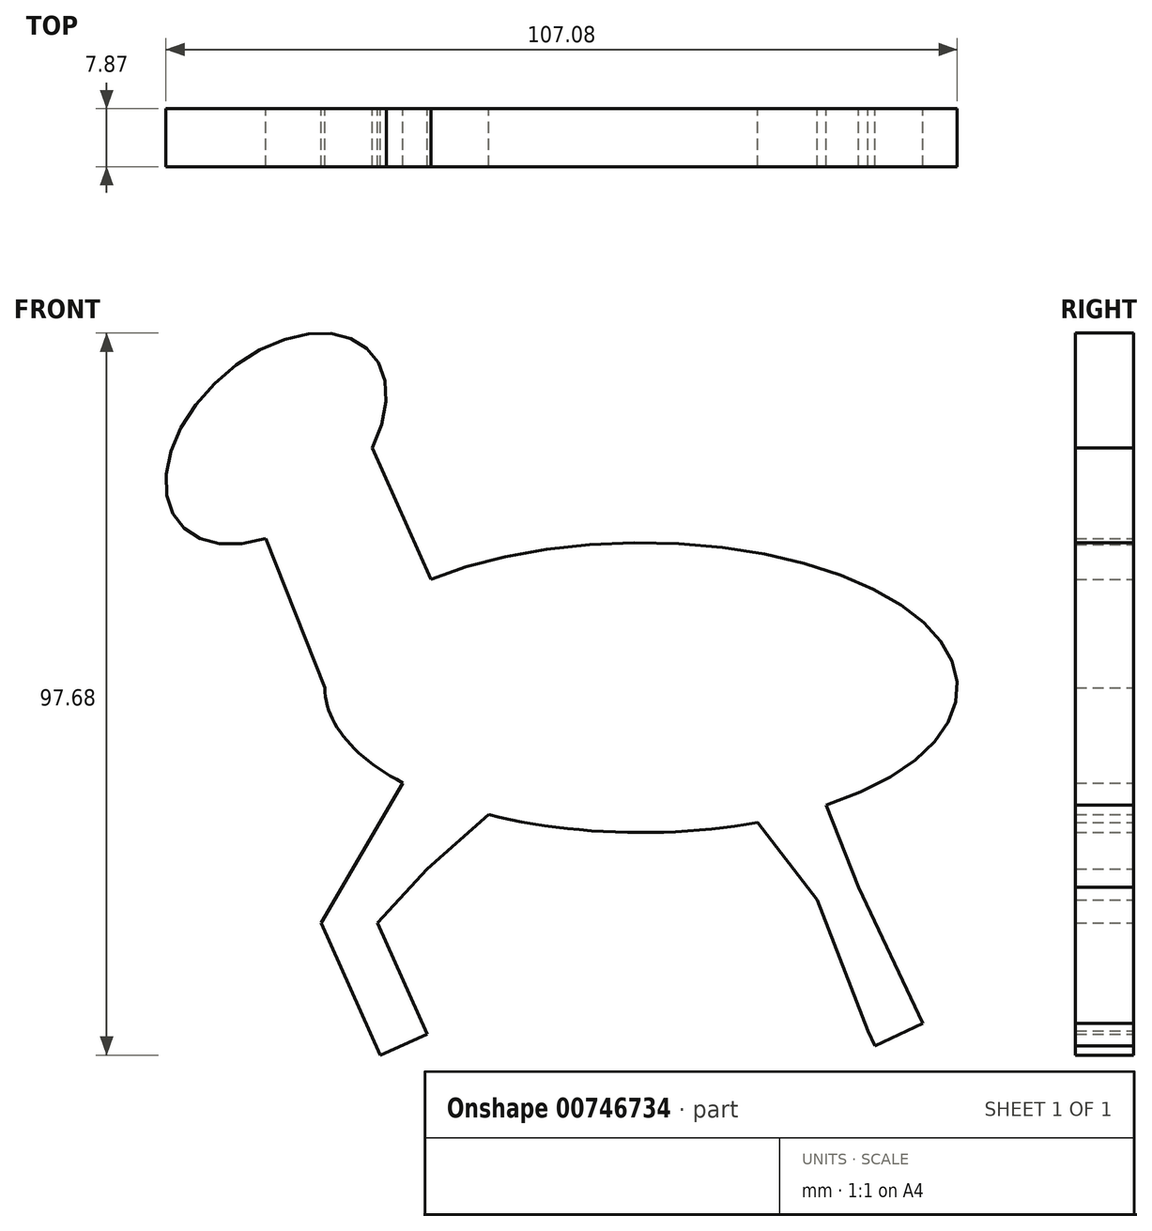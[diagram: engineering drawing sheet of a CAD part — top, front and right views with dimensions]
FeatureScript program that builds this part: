
annotation { "Feature Type Name" : "Feature", "Feature Type Description" : "" }
export const myFeature = defineFeature(function(context is Context, id is Id, definition is map)
    precondition{}
    {
        {
            var Q0;
            Q0=qCreatedBy(makeId("Front.planeOp"),FACE);
            var sketch = newSketch(context, id + "F0", { "sketchPlane" : qUnion([Q0])});
            skEllipse(sketch, "E0", {"center": v(-29.41, 9.6) * mm, "majorRadius": 42.78 * mm, "minorRadius": 19.61 * mm, "majorAxis": v(1, 0)});
            skLineSegment(sketch, "E1", {"start": v(-57.84, 24.25) * mm, "end": v(-67.48, 45.82) * mm});
            skLineSegment(sketch, "E2", {"start": v(-72.2, 9.6) * mm, "end": v(-81.94, 34.13) * mm});
            skEllipse(sketch, "E3", {"center": v(-78.8, 43.25) * mm, "majorRadius": 17.38 * mm, "minorRadius": 11.18 * mm, "majorAxis": v(0.74, 0.67)});
            skLineSegment(sketch, "E4", {"start": v(-61.65, -3.3) * mm, "end": v(-68.44, -14.97) * mm});
            skLineSegment(sketch, "E5", {"start": v(-68.44, -14.97) * mm, "end": v(-72.68, -22.27) * mm});
            skLineSegment(sketch, "E6", {"start": v(-72.68, -22.27) * mm, "end": v(-64.7, -40.13) * mm});
            skLineSegment(sketch, "E7", {"start": v(-64.7, -40.13) * mm, "end": v(-58.35, -37.3) * mm});
            skLineSegment(sketch, "E8", {"start": v(-58.35, -37.3) * mm, "end": v(-65.06, -22.27) * mm});
            skLineSegment(sketch, "E9", {"start": v(-65.06, -22.27) * mm, "end": v(-58.35, -14.97) * mm});
            skLineSegment(sketch, "E10", {"start": v(-58.35, -14.97) * mm, "end": v(-50, -7.6) * mm});
            skLineSegment(sketch, "E11", {"start": v(-4.37, -6.3) * mm, "end": v(0, -17.45) * mm});
            skLineSegment(sketch, "E12", {"start": v(1.3, -36.86) * mm, "end": v(-5.57, -19.15) * mm});
            skLineSegment(sketch, "E13", {"start": v(-5.57, -19.15) * mm, "end": v(-13.65, -8.64) * mm});
            skLineSegment(sketch, "E14", {"start": v(0, -17.45) * mm, "end": v(7.73, -33.82) * mm});
            skLineSegment(sketch, "E15", {"start": v(7.73, -33.82) * mm, "end": v(8.68, -35.83) * mm});
            skLineSegment(sketch, "E16", {"start": v(8.68, -35.83) * mm, "end": v(2.26, -38.86) * mm});
            skLineSegment(sketch, "E17", {"start": v(2.26, -38.86) * mm, "end": v(1.3, -36.86) * mm});
            skSolve(sketch);
        }
        {
            var Q0;
            Q0 = qSketchRegion(id + "F0", true);
            extrude(context, id + "F1", {"entities" : qUnion([Q0]), "depth" : 7.87 * mm, "offsetDistance" : 25.4 * mm});
        }
    });
